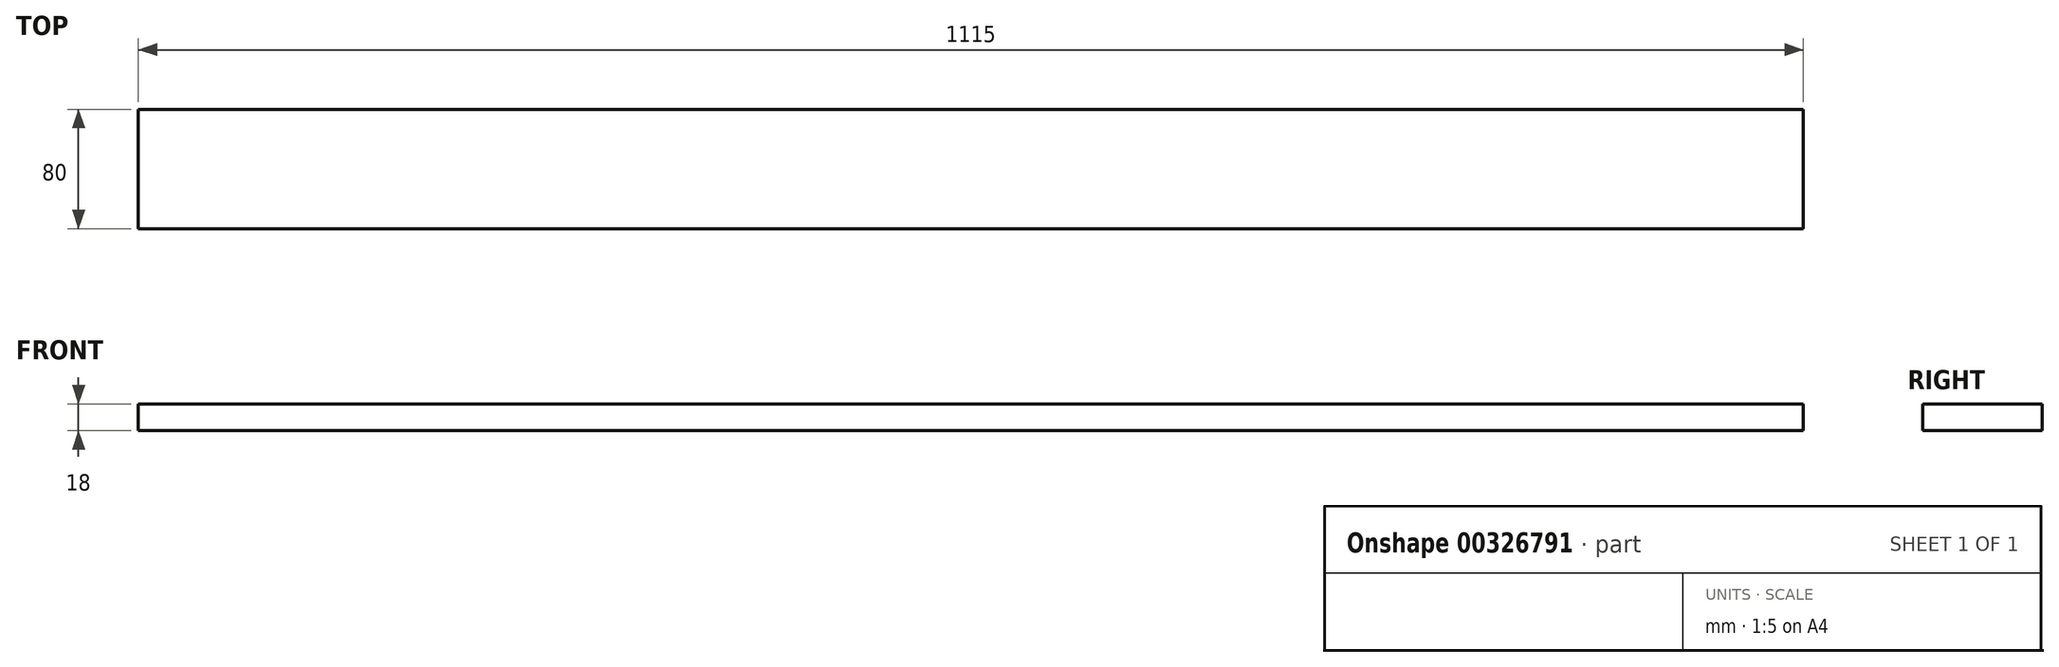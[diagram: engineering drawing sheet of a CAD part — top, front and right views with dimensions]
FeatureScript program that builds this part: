
annotation { "Feature Type Name" : "Feature", "Feature Type Description" : "" }
export const myFeature = defineFeature(function(context is Context, id is Id, definition is map)
    precondition{}
    {
        {
            var Q0;
            Q0=qCreatedBy(makeId("Top.planeOp"),FACE);
            var sketch = newSketch(context, id + "F0", { "sketchPlane" : qUnion([Q0])});
            skLineSegment(sketch, "E0.bottom", {"start": v(0, 0) * mm, "end": v(1115, 0) * mm});
            skLineSegment(sketch, "E0.top", {"start": v(0, 80) * mm, "end": v(1115, 80) * mm});
            skLineSegment(sketch, "E0.left", {"start": v(0, 0) * mm, "end": v(0, 80) * mm});
            skLineSegment(sketch, "E0.right", {"start": v(1115, 0) * mm, "end": v(1115, 80) * mm});
            skSolve(sketch);
        }
        {
            var Q0;
            Q0=qSketchRegion(id+"F0",true);
            extrude(context, id + "F1", {"entities" : qUnion([Q0]), "depth" : 18 * mm});
        }
    });
